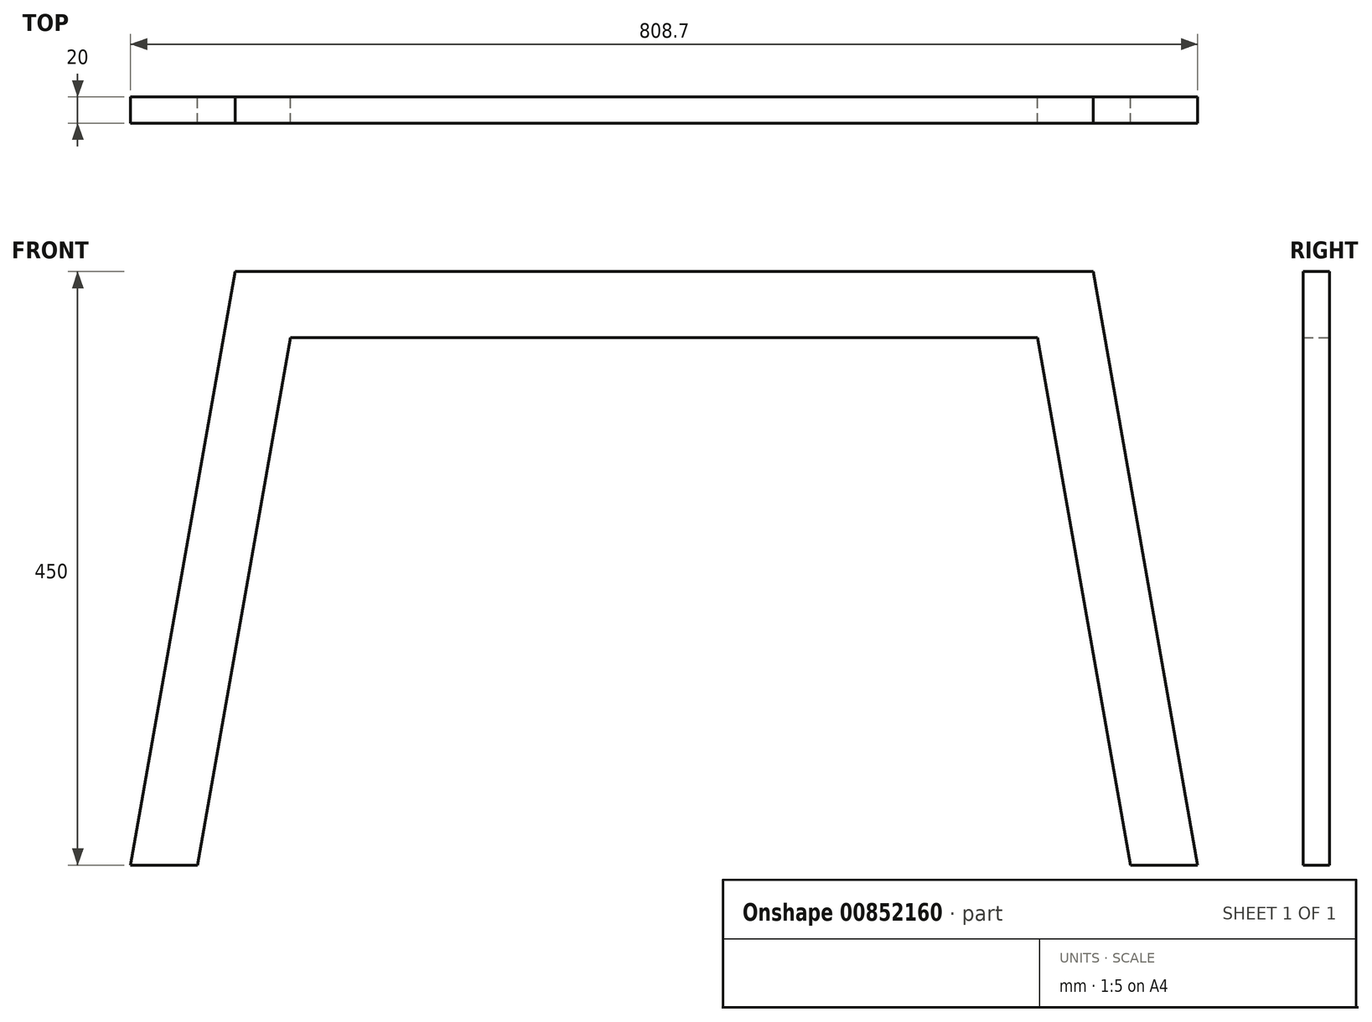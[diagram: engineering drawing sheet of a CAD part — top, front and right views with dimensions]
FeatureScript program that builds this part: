
annotation { "Feature Type Name" : "Feature", "Feature Type Description" : "" }
export const myFeature = defineFeature(function(context is Context, id is Id, definition is map)
    precondition{}
    {
        {
            var Q0;
            Q0=qCreatedBy(makeId("Front.planeOp"),FACE);
            var sketch = newSketch(context, id + "F0", { "sketchPlane" : qUnion([Q0])});
            skLineSegment(sketch, "E0", {"start": v(0, 162.2) * mm, "end": v(325, 162.2) * mm});
            skLineSegment(sketch, "E1", {"start": v(0, 112.2) * mm, "end": v(283.05, 112.2) * mm});
            skLineSegment(sketch, "E2", {"start": v(325, 162.2) * mm, "end": v(404.35, -287.8) * mm});
            skLineSegment(sketch, "E3", {"start": v(283.05, 112.2) * mm, "end": v(353.58, -287.8) * mm});
            skLineSegment(sketch, "E4", {"start": v(353.58, -287.8) * mm, "end": v(404.35, -287.8) * mm});
            skLineSegment(sketch, "E5.MirrorCS", {"start": v(0, 162.2) * mm, "end": v(-325, 162.2) * mm});
            skLineSegment(sketch, "E6.MirrorCS", {"start": v(0, 112.2) * mm, "end": v(-283.05, 112.2) * mm});
            skLineSegment(sketch, "E7.MirrorCS", {"start": v(-283.05, 112.2) * mm, "end": v(-353.58, -287.8) * mm});
            skLineSegment(sketch, "E8.MirrorCS", {"start": v(-325, 162.2) * mm, "end": v(-404.35, -287.8) * mm});
            skLineSegment(sketch, "E9.MirrorCS", {"start": v(-353.58, -287.8) * mm, "end": v(-404.35, -287.8) * mm});
            skSolve(sketch);
        }
        {
            var Q0;
            Q0=qSketchRegion(id+"F0",true);
            extrude(context, id + "F1", {"entities" : qUnion([Q0]), "depth" : 20 * mm, "offsetDistance" : 25 * mm});
        }
    });
